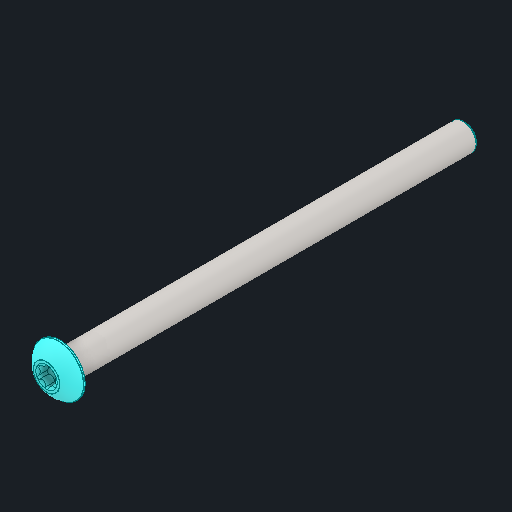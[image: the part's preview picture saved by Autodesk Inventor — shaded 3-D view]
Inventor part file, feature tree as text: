
AUTODESK INVENTOR PART (.ipt)
format: ipt  version: 2025 (Build 290162000, 162)  size: 134,656 bytes
history: native  units: in
note: dims shown in document units (in); Inventor stores cm internally (conversion verified against a paired STEP export)
features: fillet x1
ambient origin geometry x8: Origin, YZ Plane, XZ Plane, XY Plane, X Axis, Y Axis, Z Axis, Center Point
bodies: Solid1 (feature_tree)
feature tree (1):
  fillet  "Fillet1"  [1 undecoded]
note: 1 required parameter value undecoded (feature->parameter linkage not recoverable at this tier; creation-order binding heuristic only, values carry confidence <= 0.55)
